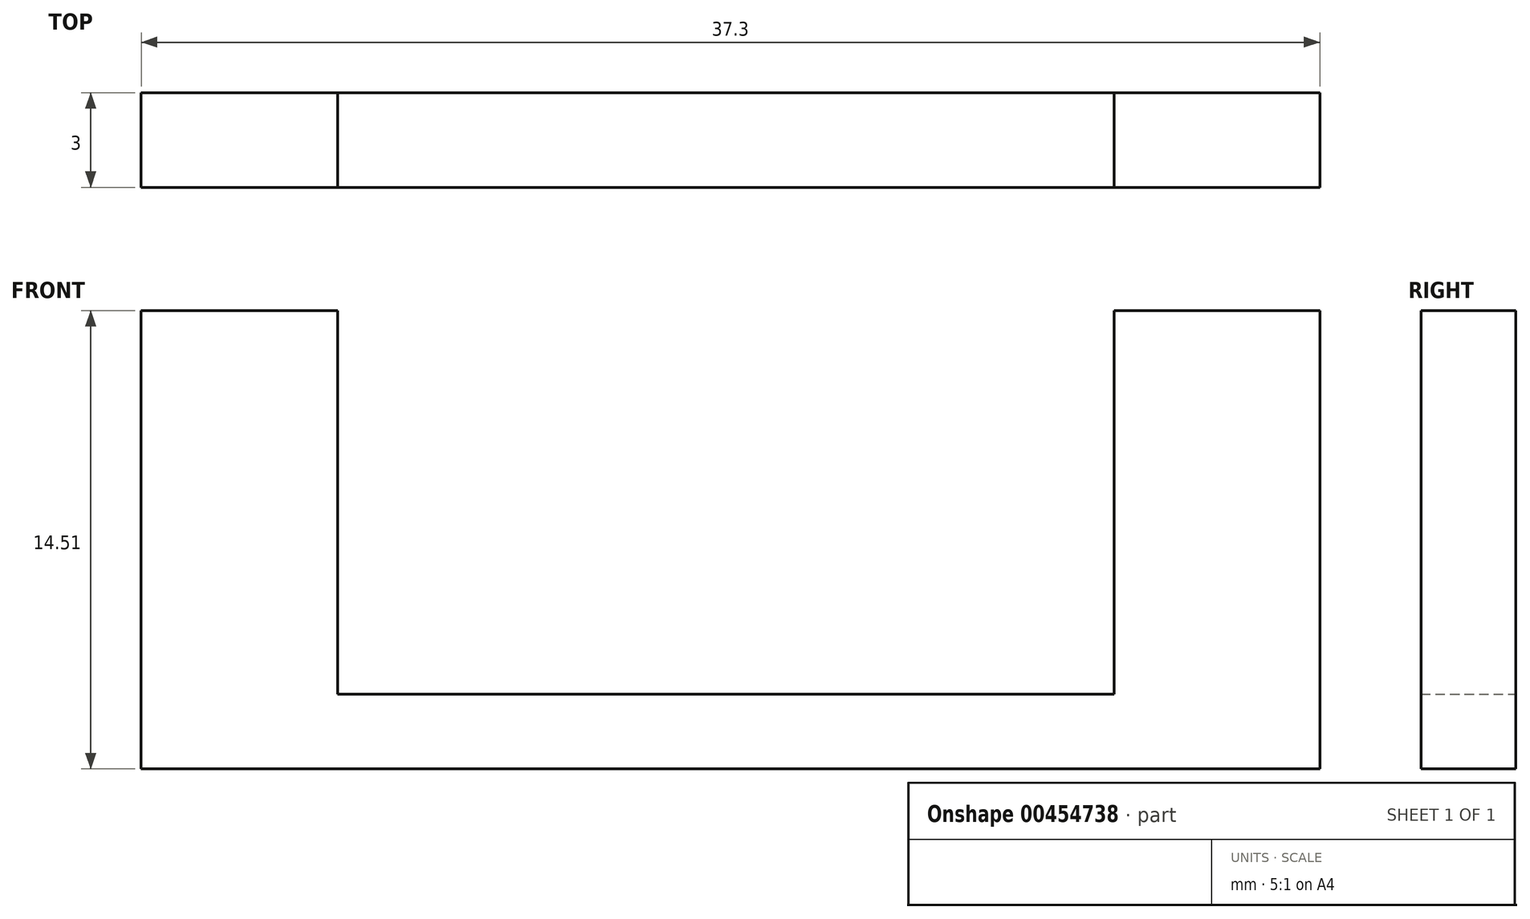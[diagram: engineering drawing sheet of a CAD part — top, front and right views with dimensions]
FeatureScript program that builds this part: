
annotation { "Feature Type Name" : "Feature", "Feature Type Description" : "" }
export const myFeature = defineFeature(function(context is Context, id is Id, definition is map)
    precondition{}
    {
        {
            var Q0;
            Q0=qCreatedBy(makeId("Front.planeOp"),FACE);
            var sketch = newSketch(context, id + "F0", { "sketchPlane" : qUnion([Q0])});
            skLineSegment(sketch, "E0", {"start": v(0, 0) * mm, "end": v(-34.34, 0) * mm});
            skLineSegment(sketch, "E1", {"start": v(-34.34, 0) * mm, "end": v(-34.34, 14.5) * mm});
            skLineSegment(sketch, "E2", {"start": v(-34.34, 14.5) * mm, "end": v(-28.13, 14.5) * mm});
            skLineSegment(sketch, "E3", {"start": v(-28.13, 14.5) * mm, "end": v(-28.13, 2.37) * mm});
            skLineSegment(sketch, "E4", {"start": v(-28.13, 2.37) * mm, "end": v(-6.22, 2.37) * mm});
            skLineSegment(sketch, "E5", {"start": v(-6.22, 2.37) * mm, "end": v(-3.55, 2.37) * mm});
            skPoint(sketch, "E5.endSnap0", {"position": v(-17.17, 2.37) * mm});
            skLineSegment(sketch, "E6", {"start": v(-3.55, 2.37) * mm, "end": v(-3.55, 14.5) * mm});
            skLineSegment(sketch, "E7", {"start": v(-3.55, 14.5) * mm, "end": v(2.96, 14.5) * mm});
            skLineSegment(sketch, "E8", {"start": v(2.96, 14.5) * mm, "end": v(2.96, 0) * mm});
            skLineSegment(sketch, "E9", {"start": v(2.96, 0) * mm, "end": v(0, 0) * mm});
            skSolve(sketch);
        }
        {
            var Q0;
            Q0=makeQuery(id+"F0.imprint","IMPRINT",FACE,{"disambiguationData":[TD([[makeQuery(id+"F0.imprint","IMPRINT",EDGE,{"derivedFrom":sQuery(id+"F0.wireOp",EDGE,"E0")}),-1.0]])]});
            extrude(context, id + "F1", {"entities" : qUnion([Q0]), "depth" : 3 * mm});
        }
    });
